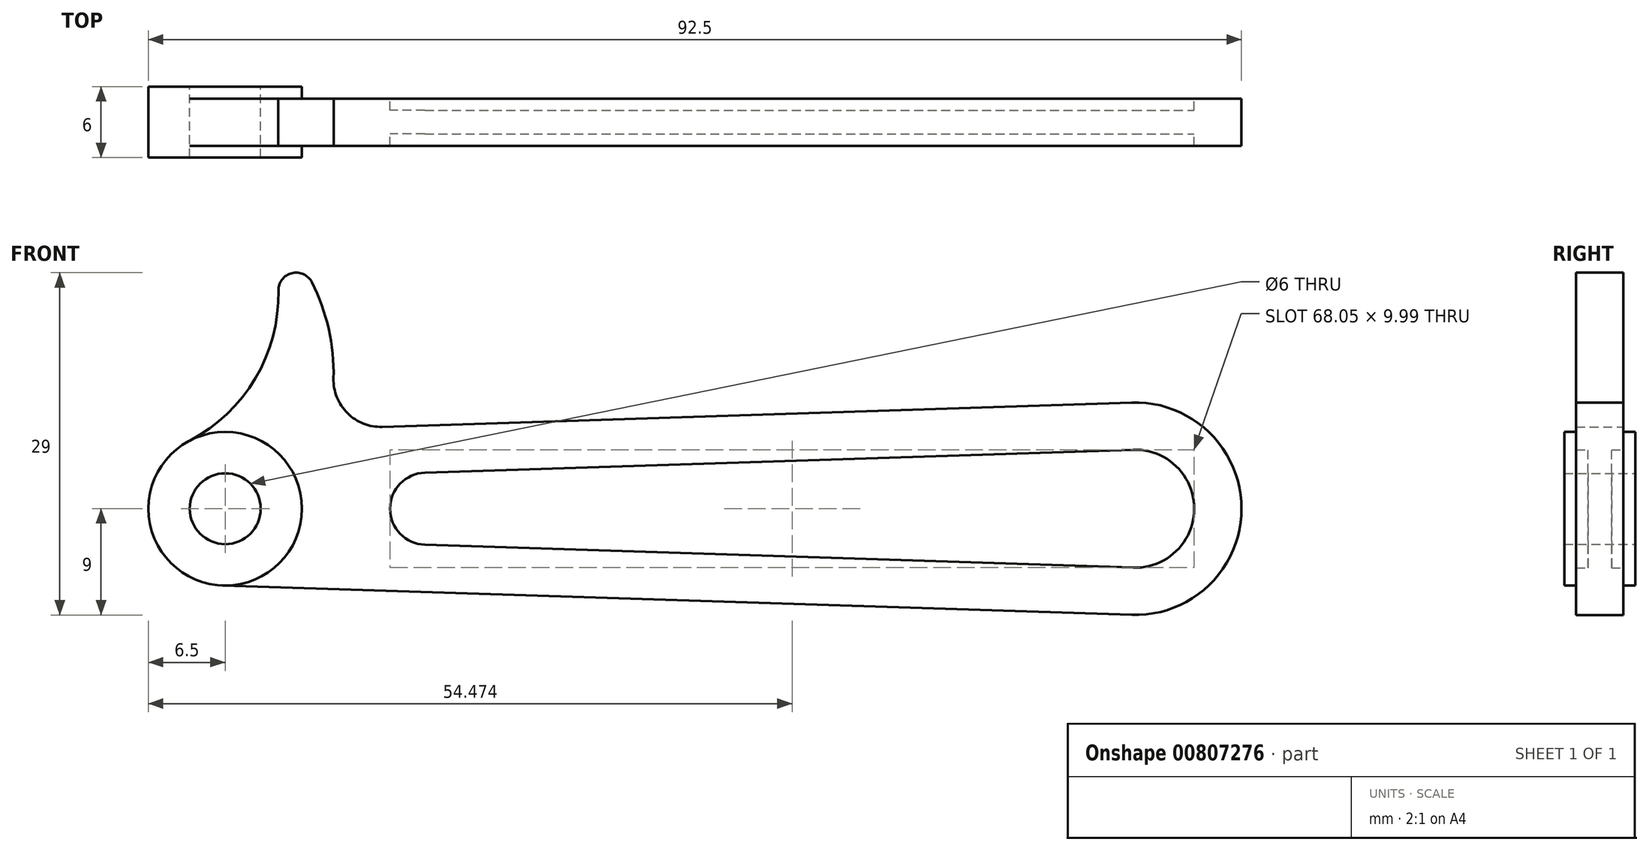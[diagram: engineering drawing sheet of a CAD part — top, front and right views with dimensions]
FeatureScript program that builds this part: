
annotation { "Feature Type Name" : "Feature", "Feature Type Description" : "" }
export const myFeature = defineFeature(function(context is Context, id is Id, definition is map)
    precondition{}
    {
        {
            var Q0;
            Q0=qCreatedBy(makeId("Front.planeOp"),FACE);
            var sketch = newSketch(context, id + "F0", { "sketchPlane" : qUnion([Q0])});
            skCircle(sketch, "E0", {"center": v(0, 0) * mm, "radius": 3 * mm});
            skCircle(sketch, "E1", {"center": v(0, 0) * mm, "radius": 6.5 * mm});
            skLineSegment(sketch, "E2", {"start": v(0, 0) * mm, "end": v(77, 0) * mm, "construction": true});
            skArc(sketch, "E3", {"start": v(76.84, -5) * mm, "mid": v(82, 0) * mm, "end": v(76.84, 5) * mm});
            skArc(sketch, "E4", {"start": v(76.7, -9) * mm, "mid": v(86, 0) * mm, "end": v(76.7, 9) * mm});
            skLineSegment(sketch, "E5", {"start": v(76.7, -9) * mm, "end": v(-0.21, -6.5) * mm});
            skLineSegment(sketch, "E6", {"start": v(16.9, -3.05) * mm, "end": v(76.84, -5) * mm});
            skLineSegment(sketch, "E7", {"start": v(17, 1.78) * mm, "end": v(17, -1.72) * mm, "construction": true});
            skArc(sketch, "E8", {"start": v(16.9, 3.05) * mm, "mid": v(13.95, 0) * mm, "end": v(16.9, -3.05) * mm});
            skLineSegment(sketch, "E9.MirrorCS", {"start": v(16.9, 3.05) * mm, "end": v(76.84, 5) * mm});
            skLineSegment(sketch, "E10.MirrorCS", {"start": v(76.7, 9) * mm, "end": v(13.3, 6.94) * mm});
            skArc(sketch, "E11", {"start": v(7.34, 19.18) * mm, "mid": v(5.64, 19.96) * mm, "end": v(4.5, 18.47) * mm});
            skLineSegment(sketch, "E12", {"start": v(-14.28, 11.5) * mm, "end": v(-2.84, 11.5) * mm, "construction": true});
            skArc(sketch, "E13", {"start": v(-4.06, -5.08) * mm, "mid": v(0.7, -3.2) * mm, "end": v(4.7, 0) * mm, "construction": true});
            skArc(sketch, "E14.trimOffspring", {"start": v(9.16, 11.04) * mm, "mid": v(8.76, 15.22) * mm, "end": v(7.34, 19.18) * mm});
            skArc(sketch, "E15", {"start": v(-3.01, 5.76) * mm, "mid": v(2.56, 11.04) * mm, "end": v(4.5, 18.47) * mm});
            skPoint(sketch, "E16.orphan", {"position": v(-0.21, 6.5) * mm});
            skPoint(sketch, "E17.visualSharp", {"position": v(8.5, 6.78) * mm});
            skArc(sketch, "E17.filletArc", {"start": v(9.16, 11.04) * mm, "mid": v(10.34, 8.1) * mm, "end": v(13.3, 6.94) * mm});
            skSolve(sketch);
        }
        {
            var Q0;
            Q0=makeQuery(id+"F0.imprint","IMPRINT",FACE,{"disambiguationData":[TD([[makeQuery(id+"F0.imprint","IMPRINT",EDGE,{"derivedFrom":sQuery(id+"F0.wireOp",EDGE,"E3")}),-1.0]])]});
            extrude(context, id + "F1", {"entities" : qUnion([Q0]), "depth" : 4 * mm, "offsetDistance" : 25 * mm, "symmetric" : true});
        }
        {
            var Q0;
            Q0=makeQuery(id+"F0.imprint","IMPRINT",FACE,{"disambiguationData":[TD([[makeQuery(id+"F0.imprint","IMPRINT",EDGE,{"derivedFrom":sQuery(id+"F0.wireOp",EDGE,"E0")}),-1.0]])]});
            extrude(context, id + "F2", {"entities" : qUnion([Q0]), "operationType" : NewBodyOperationType.ADD, "depth" : 6 * mm, "offsetDistance" : 25 * mm, "symmetric" : true});
        }
        {
            var Q0;
            Q0=makeQuery(id+"F0.imprint","IMPRINT",FACE,{"disambiguationData":[TD([[makeQuery(id+"F0.imprint","IMPRINT",EDGE,{"derivedFrom":sQuery(id+"F0.wireOp",EDGE,"E3")}),1.0]])]});
            extrude(context, id + "F3", {"entities" : qUnion([Q0]), "operationType" : NewBodyOperationType.ADD, "depth" : 2 * mm, "offsetDistance" : 25 * mm, "symmetric" : true});
        }
    });
